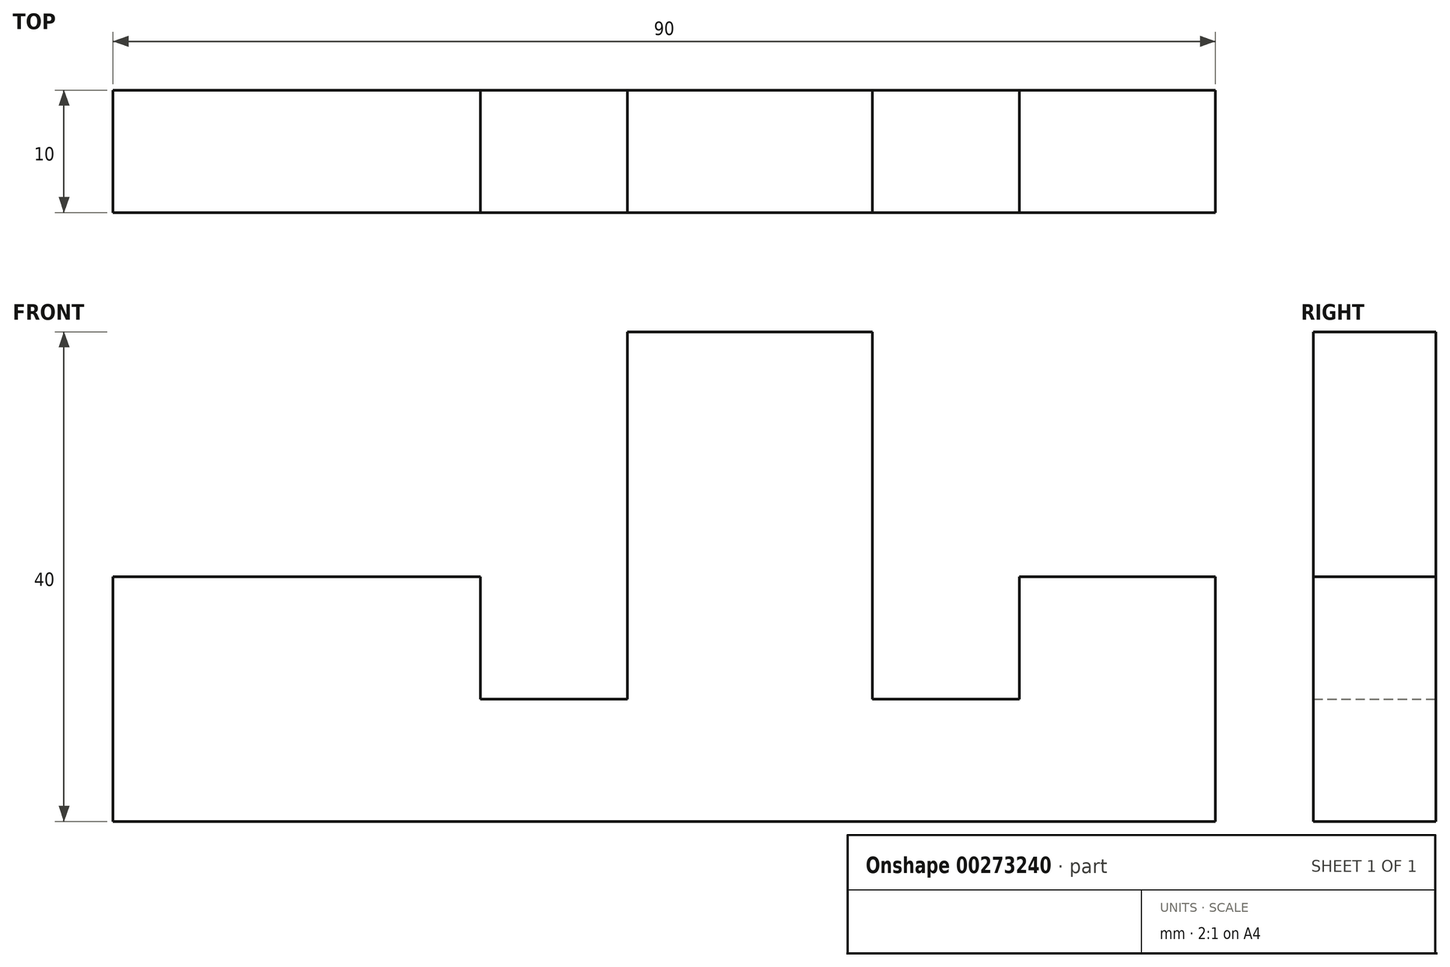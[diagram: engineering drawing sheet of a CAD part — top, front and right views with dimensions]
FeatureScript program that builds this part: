
annotation { "Feature Type Name" : "Feature", "Feature Type Description" : "" }
export const myFeature = defineFeature(function(context is Context, id is Id, definition is map)
    precondition{}
    {
        {
            var Q0;
            Q0=qCreatedBy(makeId("Front.planeOp"),FACE);
            var sketch = newSketch(context, id + "F0", { "sketchPlane" : qUnion([Q0])});
            skLineSegment(sketch, "E0", {"start": v(0, 0) * mm, "end": v(90, 0) * mm});
            skLineSegment(sketch, "E1", {"start": v(0, 0) * mm, "end": v(0, 20) * mm});
            skLineSegment(sketch, "E2", {"start": v(0, 20) * mm, "end": v(30, 20) * mm});
            skLineSegment(sketch, "E3", {"start": v(30, 20) * mm, "end": v(30, 10) * mm});
            skLineSegment(sketch, "E4", {"start": v(90, 0) * mm, "end": v(90, 20) * mm});
            skPoint(sketch, "E4.endSnap0", {"position": v(15, 20) * mm});
            skLineSegment(sketch, "E5", {"start": v(30, 10) * mm, "end": v(42, 10) * mm});
            skLineSegment(sketch, "E6", {"start": v(42, 10) * mm, "end": v(42, 40) * mm});
            skLineSegment(sketch, "E7", {"start": v(42, 40) * mm, "end": v(62, 40) * mm});
            skLineSegment(sketch, "E8", {"start": v(62, 40) * mm, "end": v(62, 10) * mm});
            skLineSegment(sketch, "E9", {"start": v(62, 10) * mm, "end": v(74, 10) * mm});
            skLineSegment(sketch, "E10", {"start": v(74, 10) * mm, "end": v(74, 20) * mm});
            skLineSegment(sketch, "E11", {"start": v(74, 20) * mm, "end": v(90, 20) * mm});
            skSolve(sketch);
        }
        {
            var Q0;
            Q0 = qSketchRegion(id + "F0", true);
            extrude(context, id + "F1", {"entities" : qUnion([Q0]), "depth" : 10 * mm});
        }
    });
